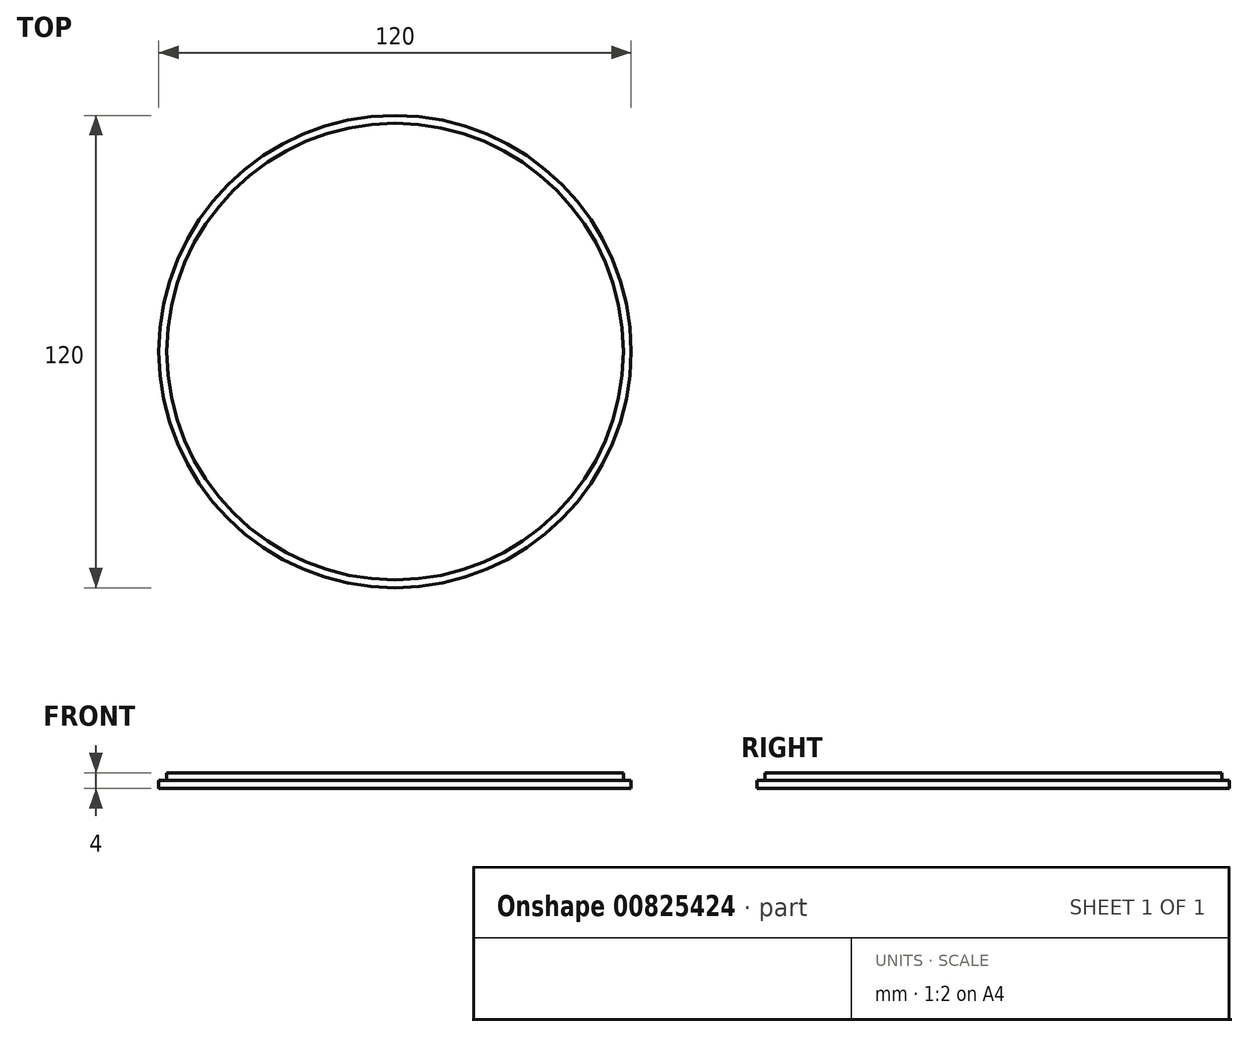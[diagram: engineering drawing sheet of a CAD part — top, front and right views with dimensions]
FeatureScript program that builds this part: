
annotation { "Feature Type Name" : "Feature", "Feature Type Description" : "" }
export const myFeature = defineFeature(function(context is Context, id is Id, definition is map)
    precondition{}
    {
        {
            var Q0;
            Q0=qCreatedBy(makeId("Top.planeOp"),FACE);
            var sketch = newSketch(context, id + "F0", { "sketchPlane" : qUnion([Q0])});
            skCircle(sketch, "E0", {"center": v(0, 0) * mm, "radius": 60 * mm});
            skSolve(sketch);
        }
        {
            var Q0;
            Q0=makeQuery(id+"F0.imprint","IMPRINT",FACE,{"disambiguationData":[TD([[makeQuery(id+"F0.imprint","IMPRINT",EDGE,{"derivedFrom":sQuery(id+"F0.wireOp",EDGE,"E0")}),1.0]])]});
            var Q1;
            Q1=sQuery(id+"F0.wireOp",EDGE,"E0");
            extrude(context, id + "F1", {"entities" : qUnion([Q0]), "surfaceOperationType" : NewSurfaceOperationType.ADD, "surfaceEntities" : qUnion([Q1]), "depth" : 2 * mm, "offsetDistance" : 25 * mm});
        }
        {
            var Q0;
            Q0=makeQuery(id+"F1.opExtrude","CAP_FACE",FACE,{"disambiguationData":[OSD([sQuery(id+"F0.wireOp",EDGE,"E0")])],"isStart":false});
            var sketch = newSketch(context, id + "F2", { "sketchPlane" : qUnion([Q0])});
            skCircle(sketch, "E1", {"center": v(0, 0) * mm, "radius": 58 * mm});
            skSolve(sketch);
        }
        {
            var Q0;
            Q0 = qSketchRegion(id + "F2", true);
            extrude(context, id + "F3", {"entities" : qUnion([Q0]), "operationType" : NewBodyOperationType.ADD, "depth" : 2 * mm, "offsetDistance" : 25 * mm});
        }
    });
